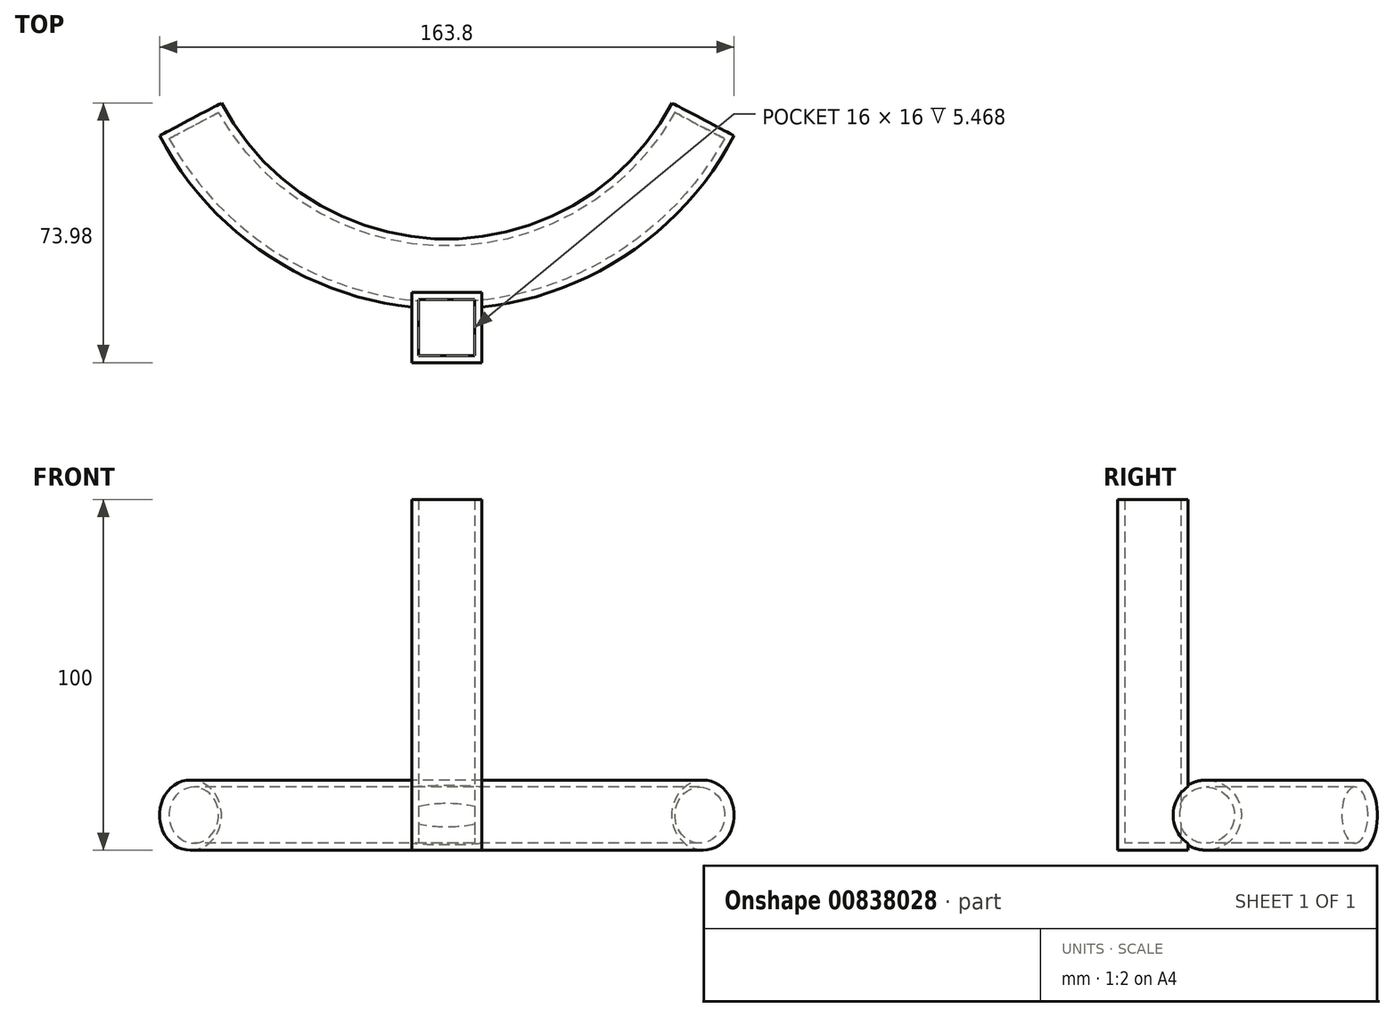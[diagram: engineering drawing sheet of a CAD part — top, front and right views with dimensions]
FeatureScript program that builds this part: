
annotation { "Feature Type Name" : "Feature", "Feature Type Description" : "" }
export const myFeature = defineFeature(function(context is Context, id is Id, definition is map)
    precondition{}
    {
        {
            var Q0;
            Q0=qCreatedBy(makeId("Right.planeOp"),FACE);
            var sketch = newSketch(context, id + "F0", { "sketchPlane" : qUnion([Q0])});
            skLineSegment(sketch, "E0", {"start": v(82.57, 23) * mm, "end": v(82.57, -17.93) * mm});
            skCircle(sketch, "E1", {"center": v(0, 0) * mm, "radius": 10 * mm});
            skSolve(sketch);
        }
        {
            var Q0;
            Q0 = qSketchRegion(id + "F0", true);
            var Q1;
            Q1=sQuery(id+"F0.wireOp",EDGE,"E0");
            revolve(context, id + "F1", {"surfaceOperationType" : NewSurfaceOperationType.NEW, "entities" : qUnion([Q0]), "axis" : qUnion([Q1]), "revolveType" : RevolveType.SYMMETRIC, "oppositeDirection" : true, "angle" : 124.45 * degree});
        }
        {
            var Q0;
            Q0=qCreatedBy(makeId("Right.planeOp"),FACE);
            var sketch = newSketch(context, id + "F2", { "sketchPlane" : qUnion([Q0])});
            skLineSegment(sketch, "E2.bottom", {"start": v(-5.23, 10) * mm, "end": v(-25.23, 10) * mm});
            skLineSegment(sketch, "E2.top", {"start": v(-5.23, -10) * mm, "end": v(-25.23, -10) * mm});
            skLineSegment(sketch, "E2.left", {"start": v(-5.23, 10) * mm, "end": v(-5.23, -10) * mm});
            skLineSegment(sketch, "E2.right", {"start": v(-25.23, 10) * mm, "end": v(-25.23, -10) * mm});
            skSolve(sketch);
        }
        {
            var Q0;
            Q0 = qSketchRegion(id + "F2", true);
            extrude(context, id + "F3", {"entities" : qUnion([Q0]), "operationType" : NewBodyOperationType.ADD, "endBound" : BoundingType.SYMMETRIC, "depth" : 20 * mm, "offsetDistance" : 25 * mm});
        }
        {
            var Q0;
            Q0=makeQuery(id+"F3.opExtrude","SWEPT_FACE",FACE,{"disambiguationData":[OSD([sQuery(id+"F2.wireOp",EDGE,"E2.bottom")])]});
            extrude(context, id + "F4", {"entities" : qUnion([Q0]), "operationType" : NewBodyOperationType.ADD, "depth" : 80 * mm, "offsetDistance" : 25 * mm});
        }
        {
            var Q0;
            Q0=makeQuery(id+"F4.opExtrude","CAP_FACE",FACE,{"disambiguationData":[OSD([sQuery(id+"F2.wireOp",EDGE,"E2.bottom")])],"isStart":false});
            shell(context, id + "F5", {"entities" : qUnion([Q0]), "thickness" : 2 * mm});
        }
    });
